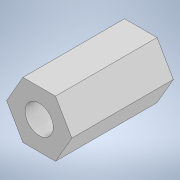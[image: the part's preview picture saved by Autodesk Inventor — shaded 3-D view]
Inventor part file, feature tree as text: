
AUTODESK INVENTOR PART (.ipt)
format: ipt  version: 2021 (Build 250183000, 183)  size: 99,328 bytes
history: native  units: mm
features: extrude x2, sketch x2
ambient origin geometry x8: Origin, YZ Plane, XZ Plane, XY Plane, X Axis, Y Axis, Z Axis, Center Point
bodies: Solid1 (feature_tree)
feature tree (4):
  extrude  "Extrusion1"  Depth=9.0mm TaperAngle=0.0deg
  extrude  "Extrusion3"  Depth=7.0mm TaperAngle=0.0deg
  sketch  "Sketch1"  dims[d0=5.0mm d1=9.0mm d2=0.0mm]
  sketch  "Sketch3"  dims[d6=2.5mm d7=7.0mm d8=0.0mm]
